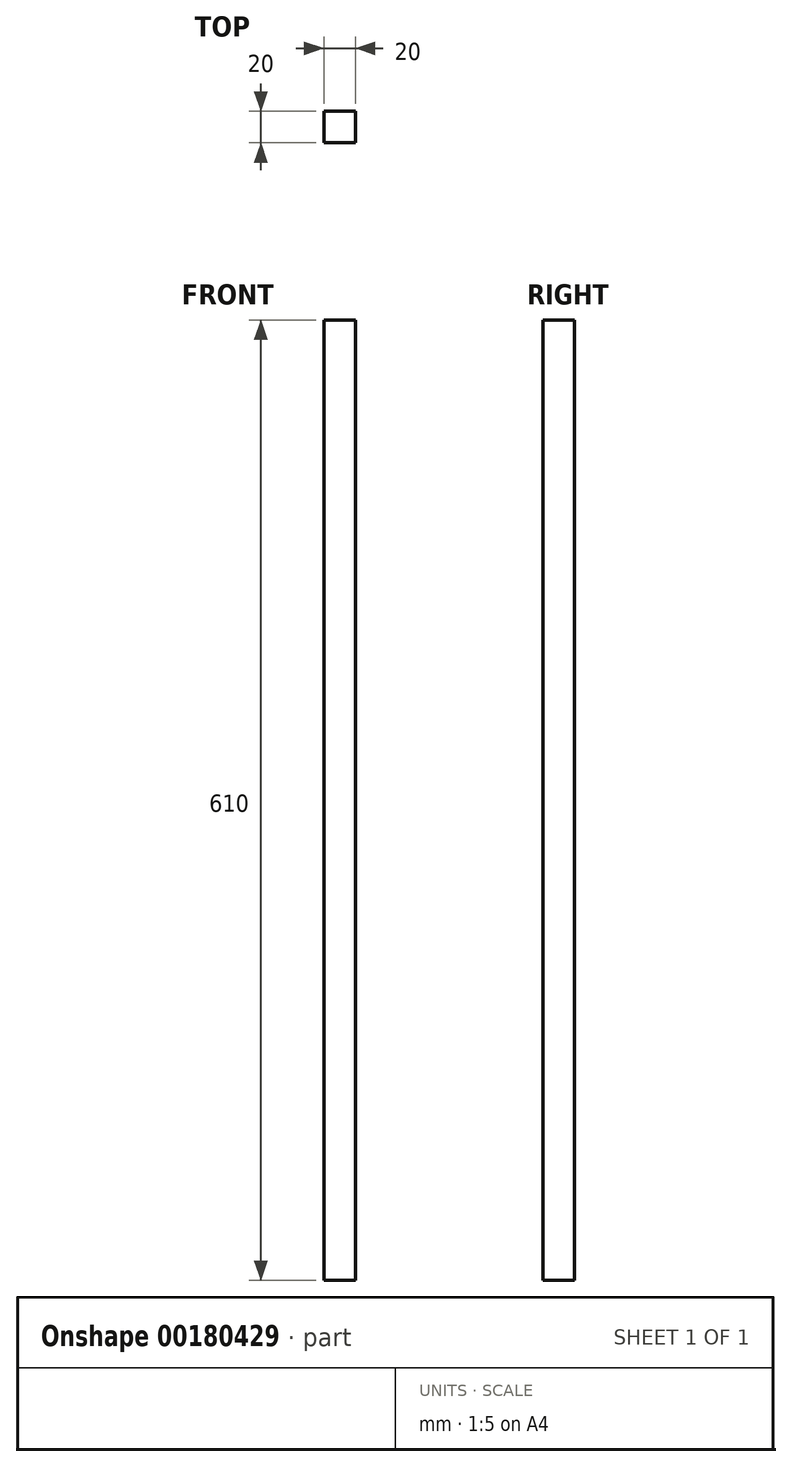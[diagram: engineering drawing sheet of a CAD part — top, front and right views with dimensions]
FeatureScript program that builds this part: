
annotation { "Feature Type Name" : "Feature", "Feature Type Description" : "" }
export const myFeature = defineFeature(function(context is Context, id is Id, definition is map)
    precondition{}
    {
        {
            var Q0;
            Q0=qCreatedBy(makeId("Top.planeOp"),FACE);
            var sketch = newSketch(context, id + "F0", { "sketchPlane" : qUnion([Q0])});
            skLineSegment(sketch, "E0.bottom", {"start": v(-78.3, -42.5) * mm, "end": v(-58.3, -42.5) * mm});
            skLineSegment(sketch, "E0.top", {"start": v(-78.3, -22.5) * mm, "end": v(-58.3, -22.5) * mm});
            skLineSegment(sketch, "E0.left", {"start": v(-78.3, -42.5) * mm, "end": v(-78.3, -22.5) * mm});
            skLineSegment(sketch, "E0.right", {"start": v(-58.3, -42.5) * mm, "end": v(-58.3, -22.5) * mm});
            skSolve(sketch);
        }
        {
            var Q0;
            Q0=makeQuery(id+"F0.imprint","IMPRINT",FACE,{"disambiguationData":[TD([[makeQuery(id+"F0.imprint","IMPRINT",EDGE,{"derivedFrom":sQuery(id+"F0.wireOp",EDGE,"E0.bottom")}),1.0]])]});
            extrude(context, id + "F1", {"entities" : qUnion([Q0]), "oppositeDirection" : true, "depth" : 610 * mm});
        }
    });
